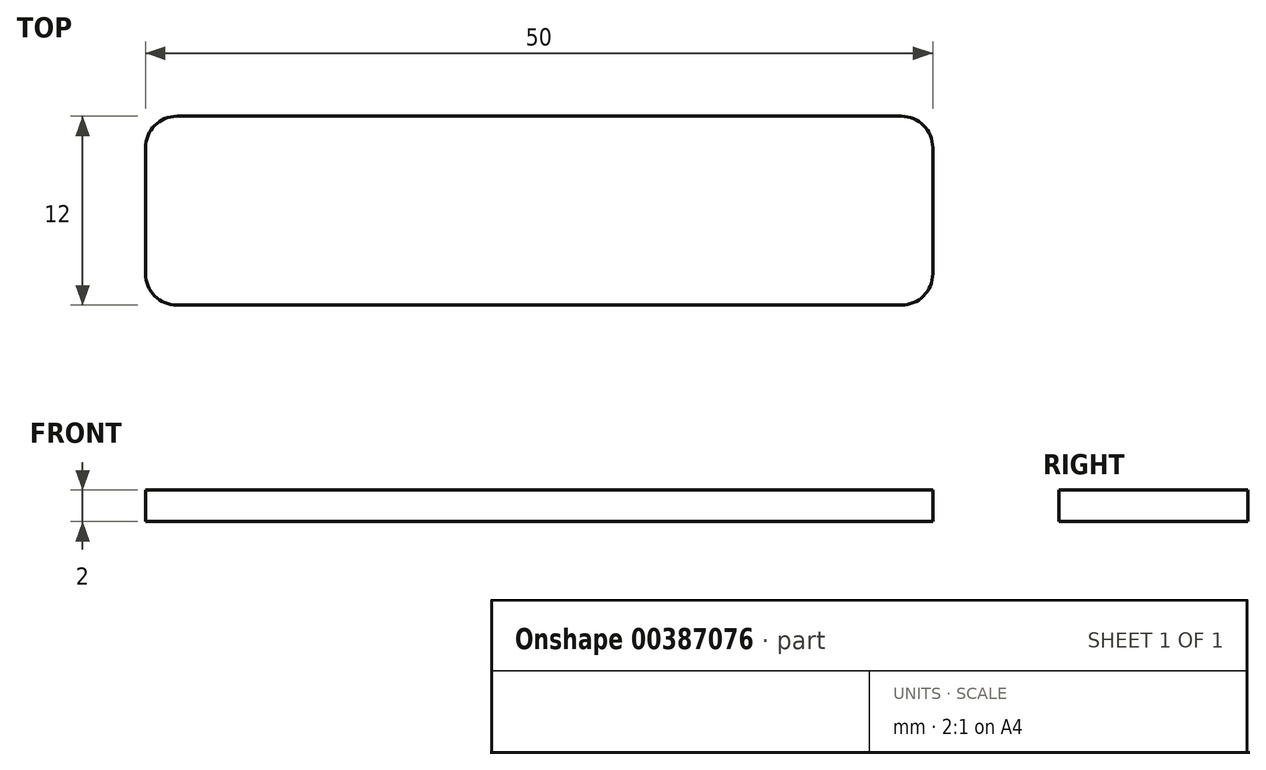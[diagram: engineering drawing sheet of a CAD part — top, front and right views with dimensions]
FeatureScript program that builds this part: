
annotation { "Feature Type Name" : "Feature", "Feature Type Description" : "" }
export const myFeature = defineFeature(function(context is Context, id is Id, definition is map)
    precondition{}
    {
        {
            var Q0;
            Q0=qCreatedBy(makeId("Top.planeOp"),FACE);
            var sketch = newSketch(context, id + "F0", { "sketchPlane" : qUnion([Q0])});
            skLineSegment(sketch, "E0.bottom", {"start": v(2, 0) * mm, "end": v(48, 0) * mm});
            skLineSegment(sketch, "E0.top", {"start": v(2, -12) * mm, "end": v(48, -12) * mm});
            skLineSegment(sketch, "E0.left", {"start": v(0, -2) * mm, "end": v(0, -10) * mm});
            skLineSegment(sketch, "E0.right", {"start": v(50, -2) * mm, "end": v(50, -10) * mm});
            skPoint(sketch, "E1.visualSharp", {"position": v(0, 0) * mm});
            skArc(sketch, "E1.filletArc", {"start": v(2, 0) * mm, "mid": v(0.59, -0.59) * mm, "end": v(0, -2) * mm});
            skPoint(sketch, "E2.visualSharp", {"position": v(50, 0) * mm});
            skArc(sketch, "E2.filletArc", {"start": v(50, -2) * mm, "mid": v(49.41, -0.59) * mm, "end": v(48, 0) * mm});
            skPoint(sketch, "E3.visualSharp", {"position": v(50, -12) * mm});
            skArc(sketch, "E3.filletArc", {"start": v(48, -12) * mm, "mid": v(49.41, -11.41) * mm, "end": v(50, -10) * mm});
            skPoint(sketch, "E4.visualSharp", {"position": v(0, -12) * mm});
            skArc(sketch, "E4.filletArc", {"start": v(0, -10) * mm, "mid": v(0.59, -11.41) * mm, "end": v(2, -12) * mm});
            skSolve(sketch);
        }
        {
            var Q0;
            Q0=makeQuery(id+"F0.imprint","IMPRINT",FACE,{"disambiguationData":[TD([[makeQuery(id+"F0.imprint","IMPRINT",EDGE,{"derivedFrom":sQuery(id+"F0.wireOp",EDGE,"E0.bottom")}),-1.0]])]});
            extrude(context, id + "F1", {"entities" : qUnion([Q0]), "depth" : 2 * mm});
        }
    });
